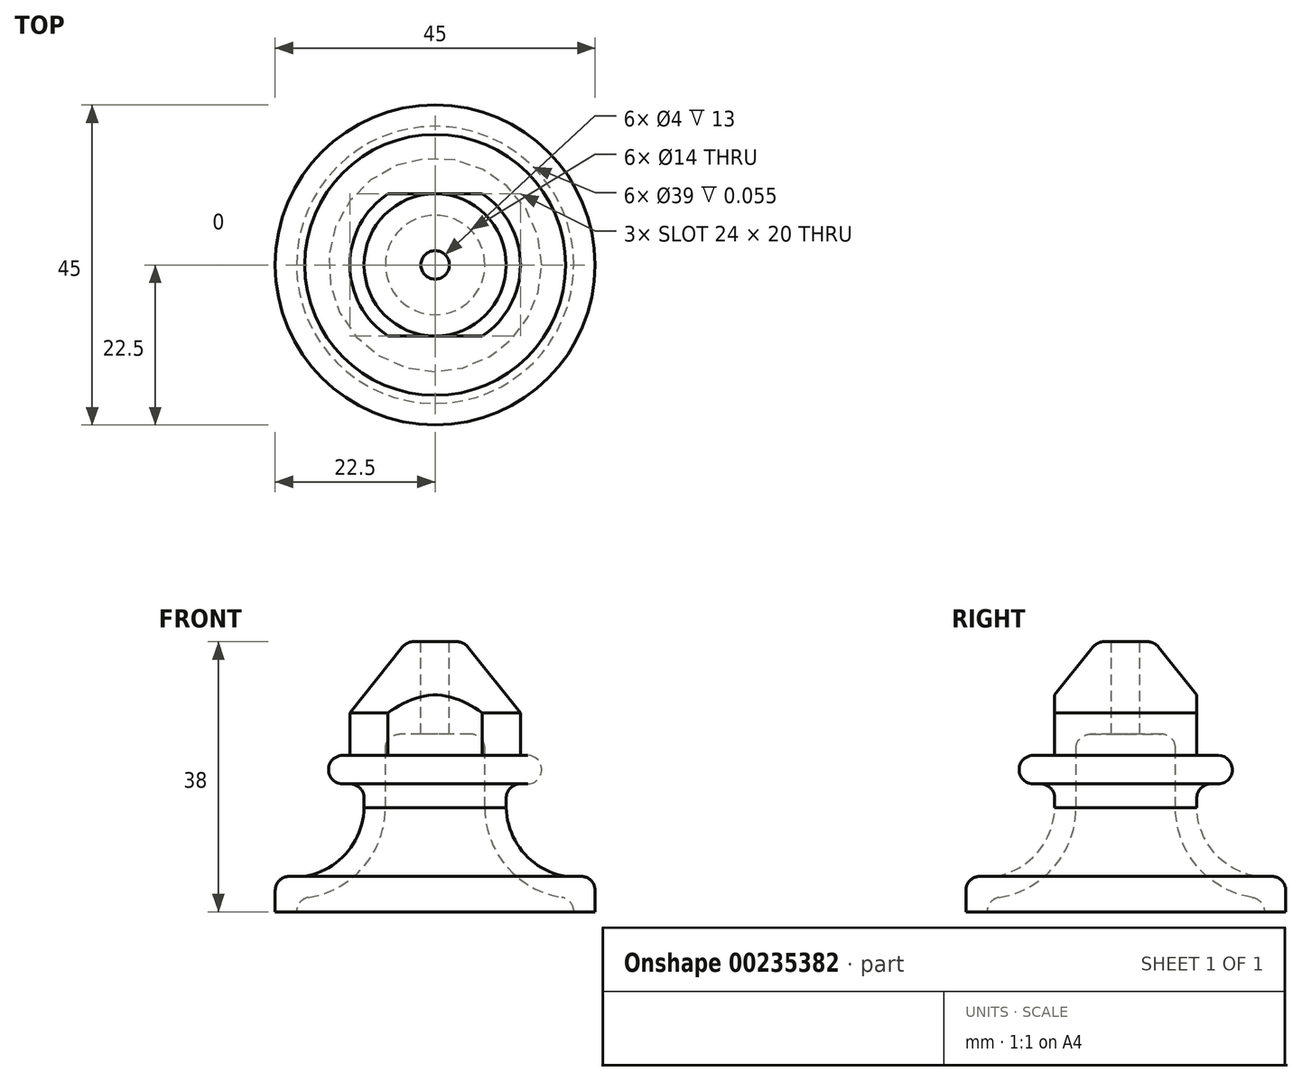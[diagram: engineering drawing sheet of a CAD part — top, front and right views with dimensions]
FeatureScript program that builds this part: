
annotation { "Feature Type Name" : "Feature", "Feature Type Description" : "" }
export const myFeature = defineFeature(function(context is Context, id is Id, definition is map)
    precondition{}
    {
        {
            var Q0;
            Q0=qCreatedBy(makeId("Front.planeOp"),FACE);
            var sketch = newSketch(context, id + "F0", { "sketchPlane" : qUnion([Q0])});
            skLineSegment(sketch, "E0", {"start": v(0, 16) * mm, "end": v(0, 3) * mm});
            skLineSegment(sketch, "E1", {"start": v(0, 16) * mm, "end": v(4, 16) * mm});
            skLineSegment(sketch, "E2", {"start": v(4, 16) * mm, "end": v(12, 6) * mm});
            skLineSegment(sketch, "E3", {"start": v(12, 6) * mm, "end": v(12, 0) * mm});
            skLineSegment(sketch, "E4", {"start": v(0, 3) * mm, "end": v(7, 3) * mm});
            skLineSegment(sketch, "E5", {"start": v(7, 3) * mm, "end": v(7, -7.34) * mm});
            skLineSegment(sketch, "E6", {"start": v(10, -4) * mm, "end": v(10, -7.34) * mm});
            skLineSegment(sketch, "E7", {"start": v(19.5, -22) * mm, "end": v(22.5, -22) * mm});
            skLineSegment(sketch, "E8", {"start": v(22.5, -22) * mm, "end": v(22.5, -17) * mm});
            skLineSegment(sketch, "E9", {"start": v(2, 16) * mm, "end": v(2, 3) * mm});
            skLineSegment(sketch, "E10", {"start": v(12, 0) * mm, "end": v(15, 0) * mm});
            skLineSegment(sketch, "E11", {"start": v(15, 0) * mm, "end": v(15, -4) * mm});
            skLineSegment(sketch, "E12", {"start": v(15, -4) * mm, "end": v(10, -4) * mm});
            skLineSegment(sketch, "E13", {"start": v(19.5, -22) * mm, "end": v(19.5, -20.12) * mm});
            skLineSegment(sketch, "E14", {"start": v(22.5, -17) * mm, "end": v(18.34, -17) * mm});
            skArc(sketch, "E15", {"start": v(10, -7.34) * mm, "mid": v(12.43, -13.67) * mm, "end": v(18.34, -17) * mm});
            skArc(sketch, "E16", {"start": v(7, -7.34) * mm, "mid": v(10.64, -16.28) * mm, "end": v(19.5, -20.12) * mm});
            skSolve(sketch);
        }
        {
            var Q0;
            {var subQ0=sQuery(id+"F0.wireOp",EDGE,"E2");Q0=makeQuery(id+"F0.imprint","IMPRINT",FACE,{"disambiguationData":[TD([[makeQuery(id+"F0.imprint","IMPRINT",EDGE,{"derivedFrom":subQ0}),-1.0]])]});}
            var Q1;
            Q1=sQuery(id+"F0.wireOp",EDGE,"E0");
            revolve(context, id + "F1", {"entities" : qUnion([Q0]), "axis" : qUnion([Q1]), "revolveType" : RevolveType.FULL});
        }
        {
            var Q0;
            Q0=makeQuery(id+"F1.opRevolve","SWEPT_EDGE",EDGE,{"disambiguationData":[OSD([sQuery(id+"F0.wireOp",EDGE,"E1"),sQuery(id+"F0.wireOp",EDGE,"E2")])]});
            var Q1;
            Q1=makeQuery(id+"F1.opRevolve","SWEPT_EDGE",EDGE,{"disambiguationData":[OSD([sQuery(id+"F0.wireOp",EDGE,"E10"),sQuery(id+"F0.wireOp",EDGE,"E11")])]});
            var Q2;
            Q2=makeQuery(id+"F1.opRevolve","SWEPT_EDGE",EDGE,{"disambiguationData":[OSD([sQuery(id+"F0.wireOp",EDGE,"E11"),sQuery(id+"F0.wireOp",EDGE,"E12")])]});
            var Q3;
            Q3=makeQuery(id+"F1.opRevolve","SWEPT_EDGE",EDGE,{"disambiguationData":[OSD([sQuery(id+"F0.wireOp",EDGE,"E8"),sQuery(id+"F0.wireOp",EDGE,"E14")])]});
            var Q4;
            Q4=makeQuery(id+"F1.opRevolve","SWEPT_EDGE",EDGE,{"disambiguationData":[OSD([sQuery(id+"F0.wireOp",EDGE,"E13"),sQuery(id+"F0.wireOp",EDGE,"E16")])]});
            var Q5;
            Q5=makeQuery(id+"F1.opRevolve","SWEPT_EDGE",EDGE,{"disambiguationData":[OSD([sQuery(id+"F0.wireOp",EDGE,"E6"),sQuery(id+"F0.wireOp",EDGE,"E12")])]});
            var Q6;
            Q6=makeQuery(id+"F1.opRevolve","SWEPT_EDGE",EDGE,{"disambiguationData":[OSD([sQuery(id+"F0.wireOp",EDGE,"E4"),sQuery(id+"F0.wireOp",EDGE,"E5")])]});
            fillet(context, id + "F2", {"entities" : qUnion([Q0, Q1, Q2, Q3, Q4, Q5, Q6]), "radius" : 2 * mm, "tangentPropagation" : true, "allowEdgeOverflow" : false});
        }
        {
            var Q0;
            Q0=qCreatedBy(makeId("Top.planeOp"),FACE);
            var sketch = newSketch(context, id + "F3", { "sketchPlane" : qUnion([Q0])});
            skCircle(sketch, "E17.0", {"center": v(0, 0) * mm, "radius": 12 * mm, "construction": true});
            skCircle(sketch, "E18.0", {"center": v(0, 0) * mm, "radius": 12 * mm});
            skLineSegment(sketch, "E19.bottom", {"start": v(-6.63, 10) * mm, "end": v(6.63, 10) * mm});
            skLineSegment(sketch, "E19.top", {"start": v(-6.63, -10) * mm, "end": v(6.63, -10) * mm});
            skLineSegment(sketch, "E19.left", {"start": v(-6.63, 10) * mm, "end": v(-6.63, -10) * mm});
            skLineSegment(sketch, "E19.right", {"start": v(6.63, 10) * mm, "end": v(6.63, -10) * mm});
            skSolve(sketch);
        }
        {
            var Q0;
            {var subQ0=sQuery(id+"F3.wireOp",EDGE,"E19.bottom");Q0=makeQuery(id+"F3.imprint","IMPRINT",FACE,{"disambiguationData":[TD([[makeQuery(id+"F3.imprint","IMPRINT",EDGE,{"derivedFrom":subQ0}),1.0]])]});}
            var Q1;
            {var subQ0=sQuery(id+"F3.wireOp",EDGE,"E19.top");Q1=makeQuery(id+"F3.imprint","IMPRINT",FACE,{"disambiguationData":[TD([[makeQuery(id+"F3.imprint","IMPRINT",EDGE,{"derivedFrom":subQ0}),-1.0]])]});}
            extrude(context, id + "F4", {"entities" : qUnion([Q0, Q1]), "operationType" : NewBodyOperationType.REMOVE, "endBound" : BoundingType.THROUGH_ALL, "depth" : 25 * mm});
        }
    });
